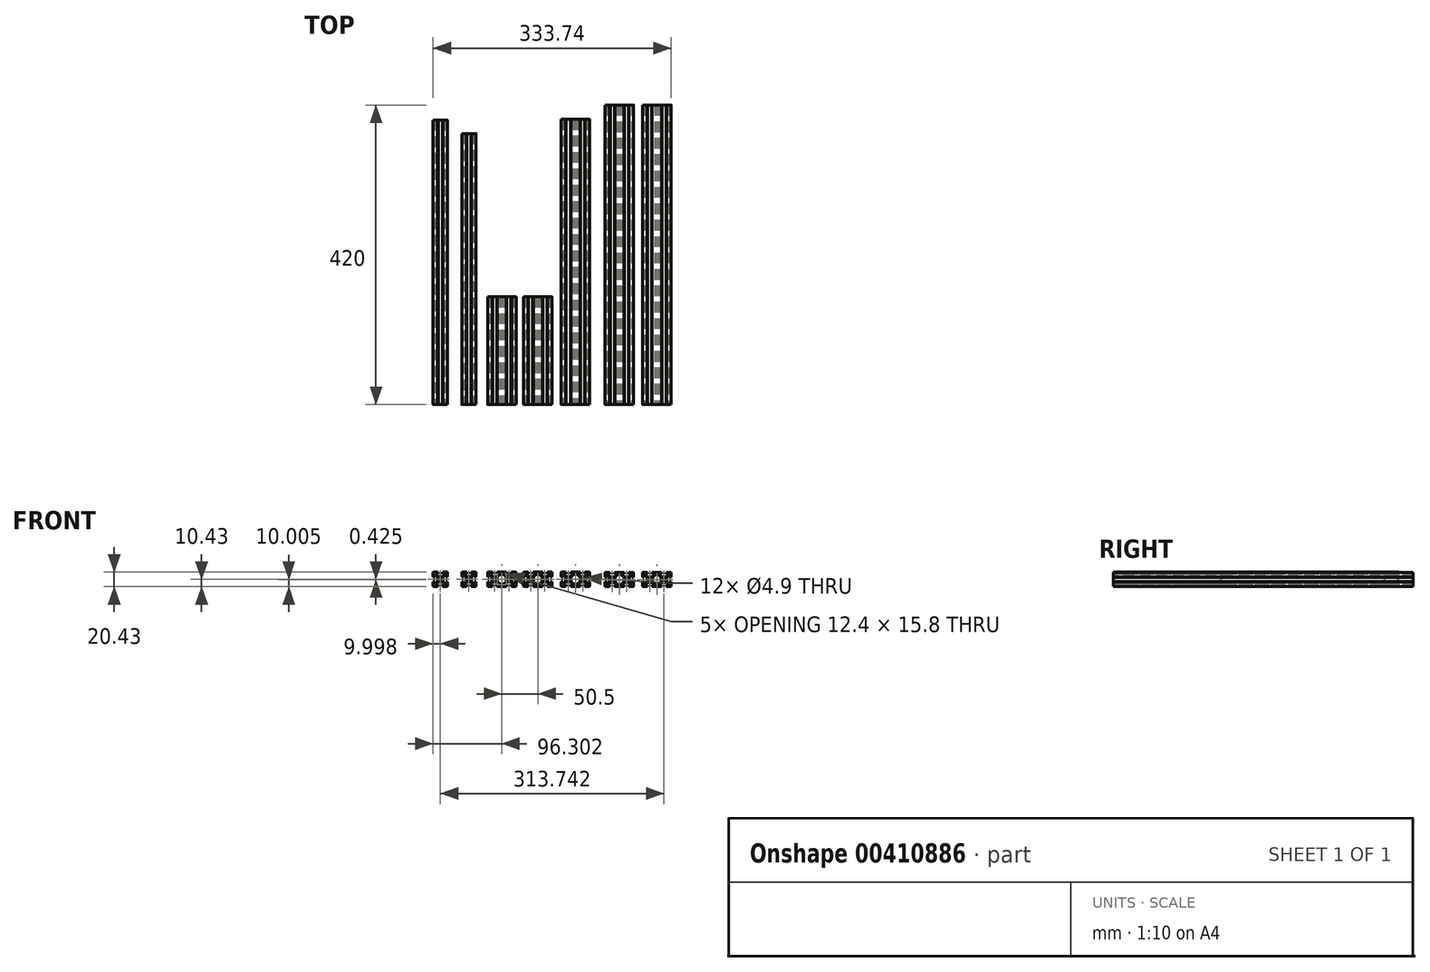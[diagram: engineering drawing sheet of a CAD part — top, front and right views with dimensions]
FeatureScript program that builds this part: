
annotation { "Feature Type Name" : "Feature", "Feature Type Description" : "" }
export const myFeature = defineFeature(function(context is Context, id is Id, definition is map)
    precondition{}
    {
        {
            var Q0;
            Q0=qCreatedBy(makeId("Front.planeOp"),FACE);
            var sketch = newSketch(context, id + "F0", { "sketchPlane" : qUnion([Q0])});
            skCircle(sketch, "E0", {"center": v(-61.2, 10) * mm, "radius": 2.45 * mm});
            skLineSegment(sketch, "E1", {"start": v(-51.2, 0.6) * mm, "end": v(-51.2, 6.4) * mm});
            skLineSegment(sketch, "E2", {"start": v(-51.2, 6.4) * mm, "end": v(-51.8, 6.4) * mm});
            skLineSegment(sketch, "E3", {"start": v(-51.8, 6.4) * mm, "end": v(-51.8, 6.95) * mm});
            skLineSegment(sketch, "E4", {"start": v(-51.8, 6.95) * mm, "end": v(-53.3, 6.95) * mm});
            skLineSegment(sketch, "E5.bottom", {"start": v(-58.31, 6.2) * mm, "end": v(-64.07, 6.2) * mm});
            skLineSegment(sketch, "E5.top", {"start": v(-58.31, 13.8) * mm, "end": v(-64.07, 13.8) * mm});
            skLineSegment(sketch, "E5.left", {"start": v(-57.4, 7.12) * mm, "end": v(-57.4, 12.88) * mm});
            skLineSegment(sketch, "E5.right", {"start": v(-65, 7.12) * mm, "end": v(-65, 12.88) * mm});
            skLineSegment(sketch, "E6", {"start": v(-57.4, 7.12) * mm, "end": v(-53.3, 3.02) * mm});
            skLineSegment(sketch, "E7", {"start": v(-58.31, 6.2) * mm, "end": v(-54.21, 2.1) * mm});
            skLineSegment(sketch, "E8", {"start": v(-53.3, 6.95) * mm, "end": v(-53.3, 3.02) * mm});
            skLineSegment(sketch, "E9.MirrorCS", {"start": v(-58.14, 2.1) * mm, "end": v(-54.21, 2.1) * mm});
            skLineSegment(sketch, "E10.MirrorCS", {"start": v(-58.14, 0.6) * mm, "end": v(-58.14, 2.1) * mm});
            skLineSegment(sketch, "E11.MirrorCS", {"start": v(-57.6, 0.6) * mm, "end": v(-58.14, 0.6) * mm});
            skLineSegment(sketch, "E12.MirrorCS", {"start": v(-57.6, 0) * mm, "end": v(-57.6, 0.6) * mm});
            skLineSegment(sketch, "E13.MirrorCS", {"start": v(-51.8, 0) * mm, "end": v(-57.6, 0) * mm});
            skLineSegment(sketch, "E14", {"start": v(-57.6, 0) * mm, "end": v(-51.8, 0) * mm});
            skLineSegment(sketch, "E15.1.0", {"start": v(-64.24, 2.1) * mm, "end": v(-68.17, 2.1) * mm});
            skLineSegment(sketch, "E15.1.1", {"start": v(-64.24, 0.6) * mm, "end": v(-64.24, 2.1) * mm});
            skLineSegment(sketch, "E15.1.2", {"start": v(-64.8, 0.6) * mm, "end": v(-64.24, 0.6) * mm});
            skLineSegment(sketch, "E15.1.3", {"start": v(-70.6, 0) * mm, "end": v(-64.8, 0) * mm});
            skLineSegment(sketch, "E15.1.4", {"start": v(-64.8, 0) * mm, "end": v(-64.8, 0.6) * mm});
            skLineSegment(sketch, "E15.1.5", {"start": v(-64.07, 6.2) * mm, "end": v(-68.17, 2.1) * mm});
            skLineSegment(sketch, "E15.1.6", {"start": v(-65, 7.12) * mm, "end": v(-69.1, 3.02) * mm});
            skLineSegment(sketch, "E15.1.7", {"start": v(-69.1, 6.95) * mm, "end": v(-69.1, 3.02) * mm});
            skLineSegment(sketch, "E15.1.8", {"start": v(-70.6, 6.95) * mm, "end": v(-69.1, 6.95) * mm});
            skLineSegment(sketch, "E15.1.9", {"start": v(-70.6, 6.4) * mm, "end": v(-70.6, 6.95) * mm});
            skLineSegment(sketch, "E15.1.10", {"start": v(-71.2, 6.4) * mm, "end": v(-70.6, 6.4) * mm});
            skLineSegment(sketch, "E15.1.11", {"start": v(-71.2, 0.6) * mm, "end": v(-71.2, 6.4) * mm});
            skLineSegment(sketch, "E15.2.0", {"start": v(-69.1, 13.05) * mm, "end": v(-69.1, 16.98) * mm});
            skLineSegment(sketch, "E15.2.1", {"start": v(-70.6, 13.05) * mm, "end": v(-69.1, 13.05) * mm});
            skLineSegment(sketch, "E15.2.2", {"start": v(-70.6, 13.6) * mm, "end": v(-70.6, 13.05) * mm});
            skLineSegment(sketch, "E15.2.3", {"start": v(-71.2, 19.4) * mm, "end": v(-71.2, 13.6) * mm});
            skLineSegment(sketch, "E15.2.4", {"start": v(-71.2, 13.6) * mm, "end": v(-70.6, 13.6) * mm});
            skLineSegment(sketch, "E15.2.5", {"start": v(-65, 12.88) * mm, "end": v(-69.1, 16.98) * mm});
            skLineSegment(sketch, "E15.2.6", {"start": v(-64.07, 13.8) * mm, "end": v(-68.17, 17.9) * mm});
            skLineSegment(sketch, "E15.2.7", {"start": v(-64.24, 17.9) * mm, "end": v(-68.17, 17.9) * mm});
            skLineSegment(sketch, "E15.2.8", {"start": v(-64.24, 19.4) * mm, "end": v(-64.24, 17.9) * mm});
            skLineSegment(sketch, "E15.2.9", {"start": v(-64.8, 19.4) * mm, "end": v(-64.24, 19.4) * mm});
            skLineSegment(sketch, "E15.2.10", {"start": v(-64.8, 20) * mm, "end": v(-64.8, 19.4) * mm});
            skLineSegment(sketch, "E15.2.11", {"start": v(-70.6, 20) * mm, "end": v(-64.8, 20) * mm});
            skLineSegment(sketch, "E15.3.0", {"start": v(-58.14, 17.9) * mm, "end": v(-54.21, 17.9) * mm});
            skLineSegment(sketch, "E15.3.1", {"start": v(-58.14, 19.4) * mm, "end": v(-58.14, 17.9) * mm});
            skLineSegment(sketch, "E15.3.2", {"start": v(-57.6, 19.4) * mm, "end": v(-58.14, 19.4) * mm});
            skLineSegment(sketch, "E15.3.3", {"start": v(-51.8, 20) * mm, "end": v(-57.6, 20) * mm});
            skLineSegment(sketch, "E15.3.4", {"start": v(-57.6, 20) * mm, "end": v(-57.6, 19.4) * mm});
            skLineSegment(sketch, "E15.3.5", {"start": v(-58.31, 13.8) * mm, "end": v(-54.21, 17.9) * mm});
            skLineSegment(sketch, "E15.3.6", {"start": v(-57.4, 12.88) * mm, "end": v(-53.3, 16.98) * mm});
            skLineSegment(sketch, "E15.3.7", {"start": v(-53.3, 13.05) * mm, "end": v(-53.3, 16.98) * mm});
            skLineSegment(sketch, "E15.3.8", {"start": v(-51.8, 13.05) * mm, "end": v(-53.3, 13.05) * mm});
            skLineSegment(sketch, "E15.3.9", {"start": v(-51.8, 13.6) * mm, "end": v(-51.8, 13.05) * mm});
            skLineSegment(sketch, "E15.3.10", {"start": v(-51.2, 13.6) * mm, "end": v(-51.8, 13.6) * mm});
            skLineSegment(sketch, "E15.3.11", {"start": v(-51.2, 19.4) * mm, "end": v(-51.2, 13.6) * mm});
            skLineSegment(sketch, "E15.anchor1", {"start": v(-59.82, 6.2) * mm, "end": v(-57.6, 0) * mm, "construction": true});
            skLineSegment(sketch, "E15.anchor2", {"start": v(-61.2, 10) * mm, "end": v(-51.2, 13.6) * mm, "construction": true});
            skPoint(sketch, "E16.orphan", {"position": v(-57.4, 13.8) * mm});
            skPoint(sketch, "E17.orphan", {"position": v(-65, 6.2) * mm});
            skArc(sketch, "E18", {"start": v(-51.8, 0) * mm, "mid": v(-51.37, 0.18) * mm, "end": v(-51.2, 0.6) * mm});
            skArc(sketch, "E19.1.6", {"start": v(-71.2, 0.6) * mm, "mid": v(-71.02, 0.18) * mm, "end": v(-70.6, 0) * mm});
            skLineSegment(sketch, "E19.1.7", {"start": v(-71.2, 6.4) * mm, "end": v(-71.2, 0.6) * mm});
            skArc(sketch, "E19.2.6", {"start": v(-70.6, 20) * mm, "mid": v(-71.02, 19.82) * mm, "end": v(-71.2, 19.4) * mm});
            skLineSegment(sketch, "E19.2.7", {"start": v(-64.8, 20) * mm, "end": v(-70.6, 20) * mm});
            skArc(sketch, "E19.3.6", {"start": v(-51.2, 19.4) * mm, "mid": v(-51.37, 19.82) * mm, "end": v(-51.8, 20) * mm});
            skLineSegment(sketch, "E19.3.7", {"start": v(-51.2, 13.6) * mm, "end": v(-51.2, 19.4) * mm});
            skLineSegment(sketch, "E19.anchor1", {"start": v(-61.2, 10) * mm, "end": v(-53.3, 3.02) * mm, "construction": true});
            skLineSegment(sketch, "E19.anchor2", {"start": v(-61.2, 10) * mm, "end": v(-54.21, 17.9) * mm, "construction": true});
            skSolve(sketch);
        }
        {
            var Q0;
            Q0=makeQuery(id+"F0.imprint","IMPRINT",FACE,{"disambiguationData":[TD([[makeQuery(id+"F0.imprint","IMPRINT",EDGE,{"derivedFrom":sQuery(id+"F0.wireOp",EDGE,"E0")}),-1.0]])]});
            extrude(context, id + "F1", {"entities" : qUnion([Q0]), "oppositeDirection" : true, "depth" : 399 * mm});
        }
        {
            var Q0;
            Q0=qCreatedBy(makeId("Front.planeOp"),FACE);
            var sketch = newSketch(context, id + "F2", { "sketchPlane" : qUnion([Q0])});
            skCircle(sketch, "E20", {"center": v(-21.06, 10) * mm, "radius": 2.45 * mm});
            skLineSegment(sketch, "E21", {"start": v(-11.06, 0.6) * mm, "end": v(-11.06, 6.4) * mm});
            skLineSegment(sketch, "E22", {"start": v(-11.06, 6.4) * mm, "end": v(-11.66, 6.4) * mm});
            skLineSegment(sketch, "E23", {"start": v(-11.66, 6.4) * mm, "end": v(-11.66, 6.94) * mm});
            skLineSegment(sketch, "E24", {"start": v(-11.66, 6.94) * mm, "end": v(-13.16, 6.94) * mm});
            skLineSegment(sketch, "E25.bottom", {"start": v(-18.18, 6.2) * mm, "end": v(-23.94, 6.2) * mm});
            skLineSegment(sketch, "E25.top", {"start": v(-18.18, 13.8) * mm, "end": v(-23.94, 13.8) * mm});
            skLineSegment(sketch, "E25.left", {"start": v(-17.26, 7.11) * mm, "end": v(-17.26, 12.87) * mm});
            skLineSegment(sketch, "E25.right", {"start": v(-24.86, 7.11) * mm, "end": v(-24.86, 12.87) * mm});
            skLineSegment(sketch, "E26", {"start": v(-17.26, 7.11) * mm, "end": v(-13.16, 3.01) * mm});
            skLineSegment(sketch, "E27", {"start": v(-18.18, 6.2) * mm, "end": v(-14.08, 2.1) * mm});
            skLineSegment(sketch, "E28", {"start": v(-13.16, 6.94) * mm, "end": v(-13.16, 3.01) * mm});
            skLineSegment(sketch, "E29.MirrorCS", {"start": v(-18.01, 2.1) * mm, "end": v(-14.08, 2.1) * mm});
            skLineSegment(sketch, "E30.MirrorCS", {"start": v(-18.01, 0.6) * mm, "end": v(-18.01, 2.1) * mm});
            skLineSegment(sketch, "E31.MirrorCS", {"start": v(-17.46, 0) * mm, "end": v(-17.46, 0.6) * mm});
            skLineSegment(sketch, "E32", {"start": v(-17.46, 0) * mm, "end": v(-11.66, 0) * mm});
            skLineSegment(sketch, "E33.1.0", {"start": v(-24.11, 2.1) * mm, "end": v(-28.04, 2.1) * mm});
            skLineSegment(sketch, "E33.1.1", {"start": v(-24.11, 0.6) * mm, "end": v(-24.11, 2.1) * mm});
            skLineSegment(sketch, "E33.1.2", {"start": v(-24.66, 0.6) * mm, "end": v(-24.11, 0.6) * mm});
            skLineSegment(sketch, "E33.1.3", {"start": v(-30.46, 0) * mm, "end": v(-24.66, 0) * mm});
            skLineSegment(sketch, "E33.1.4", {"start": v(-24.66, 0) * mm, "end": v(-24.66, 0.6) * mm});
            skLineSegment(sketch, "E33.1.5", {"start": v(-23.94, 6.2) * mm, "end": v(-28.04, 2.1) * mm});
            skLineSegment(sketch, "E33.1.6", {"start": v(-24.86, 7.11) * mm, "end": v(-28.96, 3.01) * mm});
            skLineSegment(sketch, "E33.2.0", {"start": v(-28.96, 3.01) * mm, "end": v(-28.96, 6.94) * mm});
            skLineSegment(sketch, "E33.2.3", {"start": v(-31.06, 19.4) * mm, "end": v(-31.06, 13.6) * mm});
            skLineSegment(sketch, "E33.2.5", {"start": v(-24.86, 12.87) * mm, "end": v(-28.96, 16.97) * mm});
            skLineSegment(sketch, "E33.2.6", {"start": v(-23.94, 13.8) * mm, "end": v(-28.04, 17.9) * mm});
            skLineSegment(sketch, "E33.2.11", {"start": v(-30.46, 20) * mm, "end": v(-24.66, 20) * mm});
            skLineSegment(sketch, "E33.3.0", {"start": v(-18.01, 17.9) * mm, "end": v(-14.08, 17.9) * mm});
            skLineSegment(sketch, "E33.3.1", {"start": v(-18.01, 19.4) * mm, "end": v(-18.01, 17.9) * mm});
            skLineSegment(sketch, "E33.3.2", {"start": v(-17.46, 19.4) * mm, "end": v(-18.01, 19.4) * mm});
            skLineSegment(sketch, "E33.3.3", {"start": v(-11.66, 20) * mm, "end": v(-17.46, 20) * mm});
            skLineSegment(sketch, "E33.3.4", {"start": v(-17.46, 20) * mm, "end": v(-17.46, 19.4) * mm});
            skLineSegment(sketch, "E33.3.5", {"start": v(-18.18, 13.8) * mm, "end": v(-14.08, 17.9) * mm});
            skLineSegment(sketch, "E33.3.6", {"start": v(-17.26, 12.87) * mm, "end": v(-13.16, 16.97) * mm});
            skLineSegment(sketch, "E33.3.7", {"start": v(-13.16, 13.04) * mm, "end": v(-13.16, 16.97) * mm});
            skLineSegment(sketch, "E33.3.11", {"start": v(-11.06, 19.4) * mm, "end": v(-11.06, 13.6) * mm});
            skArc(sketch, "E34", {"start": v(-11.66, 0) * mm, "mid": v(-11.24, 0.17) * mm, "end": v(-11.06, 0.6) * mm});
            skArc(sketch, "E35.1.6", {"start": v(-31.06, 0.6) * mm, "mid": v(-30.89, 0.17) * mm, "end": v(-30.46, 0) * mm});
            skLineSegment(sketch, "E35.1.7", {"start": v(-31.06, 6.4) * mm, "end": v(-31.06, 0.6) * mm});
            skLineSegment(sketch, "E35.1.8", {"start": v(-31.06, 6.4) * mm, "end": v(-30.46, 6.4) * mm});
            skLineSegment(sketch, "E35.1.9", {"start": v(-30.46, 6.4) * mm, "end": v(-30.46, 6.94) * mm});
            skLineSegment(sketch, "E35.1.10", {"start": v(-30.46, 6.94) * mm, "end": v(-28.96, 6.94) * mm});
            skLineSegment(sketch, "E35.1.11", {"start": v(-28.96, 6.94) * mm, "end": v(-28.96, 3.01) * mm});
            skLineSegment(sketch, "E35.2.1", {"start": v(-28.96, 13.04) * mm, "end": v(-28.96, 16.97) * mm});
            skLineSegment(sketch, "E35.2.2", {"start": v(-30.46, 13.04) * mm, "end": v(-28.96, 13.04) * mm});
            skLineSegment(sketch, "E35.2.3", {"start": v(-30.46, 13.6) * mm, "end": v(-30.46, 13.04) * mm});
            skLineSegment(sketch, "E35.2.4", {"start": v(-31.06, 13.6) * mm, "end": v(-30.46, 13.6) * mm});
            skArc(sketch, "E35.2.6", {"start": v(-30.46, 20) * mm, "mid": v(-30.89, 19.82) * mm, "end": v(-31.06, 19.4) * mm});
            skLineSegment(sketch, "E35.2.7", {"start": v(-24.66, 20) * mm, "end": v(-30.46, 20) * mm});
            skLineSegment(sketch, "E35.2.8", {"start": v(-24.66, 20) * mm, "end": v(-24.66, 19.4) * mm});
            skLineSegment(sketch, "E35.2.9", {"start": v(-24.66, 19.4) * mm, "end": v(-24.11, 19.4) * mm});
            skLineSegment(sketch, "E35.2.10", {"start": v(-24.11, 19.4) * mm, "end": v(-24.11, 17.9) * mm});
            skLineSegment(sketch, "E35.2.11", {"start": v(-24.11, 17.9) * mm, "end": v(-28.04, 17.9) * mm});
            skArc(sketch, "E35.3.6", {"start": v(-11.06, 19.4) * mm, "mid": v(-11.24, 19.82) * mm, "end": v(-11.66, 20) * mm});
            skLineSegment(sketch, "E35.3.7", {"start": v(-11.06, 13.6) * mm, "end": v(-11.06, 19.4) * mm});
            skLineSegment(sketch, "E35.3.8", {"start": v(-11.06, 13.6) * mm, "end": v(-11.66, 13.6) * mm});
            skLineSegment(sketch, "E35.3.9", {"start": v(-11.66, 13.6) * mm, "end": v(-11.66, 13.04) * mm});
            skLineSegment(sketch, "E35.3.10", {"start": v(-11.66, 13.04) * mm, "end": v(-13.16, 13.04) * mm});
            skLineSegment(sketch, "E35.3.11", {"start": v(-13.16, 3.01) * mm, "end": v(-13.16, 6.94) * mm});
            skLineSegment(sketch, "E36.trimOffspring", {"start": v(-31.06, 6.4) * mm, "end": v(-31.06, 2.99) * mm});
            skLineSegment(sketch, "E37.trimOffspring", {"start": v(-11.06, 6.4) * mm, "end": v(-11.06, 2.99) * mm});
            skLineSegment(sketch, "E38.trimOffspring", {"start": v(-14.08, 17.9) * mm, "end": v(-18.01, 17.9) * mm});
            skLineSegment(sketch, "E39", {"start": v(-17.46, 0.6) * mm, "end": v(-18.01, 0.6) * mm});
            skLineSegment(sketch, "E40.trimOffspring", {"start": v(-14.08, 2.1) * mm, "end": v(-18.18, 6.2) * mm});
            skSolve(sketch);
        }
        {
            var Q0;
            Q0=makeQuery(id+"F2.imprint","IMPRINT",FACE,{"disambiguationData":[TD([[makeQuery(id+"F2.imprint","IMPRINT",EDGE,{"derivedFrom":sQuery(id+"F2.wireOp",EDGE,"E20")}),-1.0]])]});
            extrude(context, id + "F3", {"entities" : qUnion([Q0]), "oppositeDirection" : true, "depth" : 380 * mm});
        }
        {
            var Q0;
            Q0=qCreatedBy(makeId("Front.planeOp"),FACE);
            var sketch = newSketch(context, id + "F4", { "sketchPlane" : qUnion([Q0])});
            skCircle(sketch, "E41", {"center": v(15.11, 10) * mm, "radius": 2.45 * mm});
            skLineSegment(sketch, "E42.bottom", {"start": v(18, 6.2) * mm, "end": v(12.23, 6.2) * mm});
            skLineSegment(sketch, "E42.top", {"start": v(18, 13.8) * mm, "end": v(12.23, 13.8) * mm});
            skLineSegment(sketch, "E42.left", {"start": v(18.91, 7.12) * mm, "end": v(18.91, 12.88) * mm});
            skLineSegment(sketch, "E42.right", {"start": v(11.31, 7.12) * mm, "end": v(11.31, 12.88) * mm});
            skLineSegment(sketch, "E43", {"start": v(18.91, 7.12) * mm, "end": v(23.01, 3.02) * mm});
            skLineSegment(sketch, "E44", {"start": v(18, 6.2) * mm, "end": v(22.1, 2.1) * mm});
            skLineSegment(sketch, "E45.MirrorCS", {"start": v(18.16, 2.1) * mm, "end": v(22.1, 2.1) * mm});
            skLineSegment(sketch, "E46.MirrorCS", {"start": v(18.16, 0.6) * mm, "end": v(18.16, 2.1) * mm});
            skLineSegment(sketch, "E47.MirrorCS", {"start": v(18.71, 0) * mm, "end": v(18.71, 0.6) * mm});
            skLineSegment(sketch, "E48", {"start": v(18.71, 0) * mm, "end": v(24.51, 0) * mm});
            skLineSegment(sketch, "E49.1.0", {"start": v(12.06, 2.1) * mm, "end": v(8.13, 2.1) * mm});
            skLineSegment(sketch, "E49.1.1", {"start": v(12.06, 0.6) * mm, "end": v(12.06, 2.1) * mm});
            skLineSegment(sketch, "E49.1.2", {"start": v(11.51, 0.6) * mm, "end": v(12.06, 0.6) * mm});
            skLineSegment(sketch, "E49.1.3", {"start": v(5.71, 0) * mm, "end": v(11.51, 0) * mm});
            skLineSegment(sketch, "E49.1.4", {"start": v(11.51, 0) * mm, "end": v(11.51, 0.6) * mm});
            skLineSegment(sketch, "E49.1.5", {"start": v(12.23, 6.2) * mm, "end": v(8.13, 2.1) * mm});
            skLineSegment(sketch, "E49.1.6", {"start": v(11.31, 7.12) * mm, "end": v(7.21, 3.02) * mm});
            skLineSegment(sketch, "E49.2.0", {"start": v(7.21, 3.02) * mm, "end": v(7.21, 6.95) * mm});
            skLineSegment(sketch, "E49.2.3", {"start": v(5.11, 19.4) * mm, "end": v(5.11, 13.6) * mm});
            skLineSegment(sketch, "E49.2.5", {"start": v(11.31, 12.88) * mm, "end": v(7.21, 16.98) * mm});
            skLineSegment(sketch, "E49.2.6", {"start": v(12.23, 13.8) * mm, "end": v(8.13, 17.9) * mm});
            skLineSegment(sketch, "E49.2.11", {"start": v(5.71, 20) * mm, "end": v(11.51, 20) * mm});
            skLineSegment(sketch, "E49.3.0", {"start": v(18.16, 17.9) * mm, "end": v(22.1, 17.9) * mm});
            skLineSegment(sketch, "E49.3.1", {"start": v(18.16, 19.4) * mm, "end": v(18.16, 17.9) * mm});
            skLineSegment(sketch, "E49.3.2", {"start": v(18.71, 19.4) * mm, "end": v(18.16, 19.4) * mm});
            skLineSegment(sketch, "E49.3.3", {"start": v(24.51, 20) * mm, "end": v(18.71, 20) * mm});
            skLineSegment(sketch, "E49.3.4", {"start": v(18.71, 20) * mm, "end": v(18.71, 19.4) * mm});
            skLineSegment(sketch, "E49.3.5", {"start": v(18, 13.8) * mm, "end": v(22.1, 17.9) * mm});
            skLineSegment(sketch, "E49.3.6", {"start": v(18.91, 12.88) * mm, "end": v(23.01, 16.98) * mm});
            skArc(sketch, "E50.1.6", {"start": v(5.11, 0.6) * mm, "mid": v(5.29, 0.18) * mm, "end": v(5.71, 0) * mm});
            skLineSegment(sketch, "E50.1.7", {"start": v(5.11, 6.4) * mm, "end": v(5.11, 0.6) * mm});
            skLineSegment(sketch, "E50.1.8", {"start": v(5.11, 6.4) * mm, "end": v(5.71, 6.4) * mm});
            skLineSegment(sketch, "E50.1.9", {"start": v(5.71, 6.4) * mm, "end": v(5.71, 6.95) * mm});
            skLineSegment(sketch, "E50.1.10", {"start": v(5.71, 6.95) * mm, "end": v(7.21, 6.95) * mm});
            skLineSegment(sketch, "E50.1.11", {"start": v(7.21, 6.95) * mm, "end": v(7.21, 3.02) * mm});
            skLineSegment(sketch, "E50.2.1", {"start": v(7.21, 13.05) * mm, "end": v(7.21, 16.98) * mm});
            skLineSegment(sketch, "E50.2.2", {"start": v(5.71, 13.05) * mm, "end": v(7.21, 13.05) * mm});
            skLineSegment(sketch, "E50.2.3", {"start": v(5.71, 13.6) * mm, "end": v(5.71, 13.05) * mm});
            skLineSegment(sketch, "E50.2.4", {"start": v(5.11, 13.6) * mm, "end": v(5.71, 13.6) * mm});
            skArc(sketch, "E50.2.6", {"start": v(5.71, 20) * mm, "mid": v(5.29, 19.82) * mm, "end": v(5.11, 19.4) * mm});
            skLineSegment(sketch, "E50.2.7", {"start": v(11.51, 20) * mm, "end": v(5.71, 20) * mm});
            skLineSegment(sketch, "E50.2.8", {"start": v(11.51, 20) * mm, "end": v(11.51, 19.4) * mm});
            skLineSegment(sketch, "E50.2.9", {"start": v(11.51, 19.4) * mm, "end": v(12.06, 19.4) * mm});
            skLineSegment(sketch, "E50.2.10", {"start": v(12.06, 19.4) * mm, "end": v(12.06, 17.9) * mm});
            skLineSegment(sketch, "E50.2.11", {"start": v(12.06, 17.9) * mm, "end": v(8.13, 17.9) * mm});
            skLineSegment(sketch, "E51.trimOffspring", {"start": v(5.11, 6.4) * mm, "end": v(5.11, 3) * mm});
            skLineSegment(sketch, "E52.trimOffspring", {"start": v(22.1, 17.9) * mm, "end": v(18.16, 17.9) * mm});
            skLineSegment(sketch, "E53", {"start": v(18.71, 0.6) * mm, "end": v(18.16, 0.6) * mm});
            skLineSegment(sketch, "E54.trimOffspring", {"start": v(22.1, 2.1) * mm, "end": v(18, 6.2) * mm});
            skLineSegment(sketch, "E55.MirrorCS", {"start": v(38.16, 0.6) * mm, "end": v(38.16, 2.1) * mm});
            skLineSegment(sketch, "E56.MirrorCS", {"start": v(31.51, 19.4) * mm, "end": v(32.06, 19.4) * mm});
            skLineSegment(sketch, "E57.MirrorCS", {"start": v(38.71, 0.6) * mm, "end": v(38.16, 0.6) * mm});
            skLineSegment(sketch, "E58.MirrorCS", {"start": v(38.71, 0) * mm, "end": v(38.71, 0.6) * mm});
            skLineSegment(sketch, "E59.MirrorCS", {"start": v(31.51, 20) * mm, "end": v(31.51, 19.4) * mm});
            skLineSegment(sketch, "E60.MirrorCS", {"start": v(32.06, 19.4) * mm, "end": v(32.06, 17.9) * mm});
            skLineSegment(sketch, "E61.MirrorCS", {"start": v(38.71, 20) * mm, "end": v(38.71, 19.4) * mm});
            skArc(sketch, "E62.MirrorCS", {"start": v(44.51, 20) * mm, "mid": v(44.94, 19.82) * mm, "end": v(45.11, 19.4) * mm});
            skLineSegment(sketch, "E63.MirrorCS", {"start": v(45.11, 13.6) * mm, "end": v(44.51, 13.6) * mm});
            skLineSegment(sketch, "E64.MirrorCS", {"start": v(38.71, 19.4) * mm, "end": v(38.16, 19.4) * mm});
            skLineSegment(sketch, "E65.MirrorCS", {"start": v(45.11, 6.4) * mm, "end": v(44.51, 6.4) * mm});
            skLineSegment(sketch, "E66.MirrorCS", {"start": v(44.51, 13.05) * mm, "end": v(43.01, 13.05) * mm});
            skLineSegment(sketch, "E67.MirrorCS", {"start": v(32.06, 0.6) * mm, "end": v(32.06, 2.1) * mm});
            skLineSegment(sketch, "E68.MirrorCS", {"start": v(38.16, 19.4) * mm, "end": v(38.16, 17.9) * mm});
            skArc(sketch, "E69.MirrorCS", {"start": v(45.11, 0.6) * mm, "mid": v(44.94, 0.18) * mm, "end": v(44.51, 0) * mm});
            skLineSegment(sketch, "E70.MirrorCS", {"start": v(32.06, 17.9) * mm, "end": v(28.13, 17.9) * mm});
            skLineSegment(sketch, "E71.MirrorCS", {"start": v(31.51, 0.6) * mm, "end": v(32.06, 0.6) * mm});
            skLineSegment(sketch, "E72.MirrorCS", {"start": v(44.51, 6.4) * mm, "end": v(44.51, 6.95) * mm});
            skLineSegment(sketch, "E73.MirrorCS", {"start": v(44.51, 6.95) * mm, "end": v(43.01, 6.95) * mm});
            skLineSegment(sketch, "E74.MirrorCS", {"start": v(31.51, 0) * mm, "end": v(31.51, 0.6) * mm});
            skLineSegment(sketch, "E75.MirrorCS", {"start": v(44.51, 13.6) * mm, "end": v(44.51, 13.05) * mm});
            skLineSegment(sketch, "E76.MirrorCS", {"start": v(32.23, 13.8) * mm, "end": v(28.13, 17.9) * mm});
            skPoint(sketch, "E77.MirrorP", {"position": v(35.11, 10) * mm});
            skLineSegment(sketch, "E78.MirrorCS", {"start": v(43.01, 13.05) * mm, "end": v(43.01, 16.98) * mm});
            skLineSegment(sketch, "E79.MirrorCS", {"start": v(44.51, 0) * mm, "end": v(38.71, 0) * mm});
            skLineSegment(sketch, "E80.MirrorCS", {"start": v(38.16, 17.9) * mm, "end": v(42.1, 17.9) * mm});
            skLineSegment(sketch, "E81.MirrorCS", {"start": v(38.91, 7.12) * mm, "end": v(43.01, 3.02) * mm});
            skLineSegment(sketch, "E82.MirrorCS", {"start": v(38.16, 2.1) * mm, "end": v(42.1, 2.1) * mm});
            skLineSegment(sketch, "E83.MirrorCS", {"start": v(38.91, 12.88) * mm, "end": v(43.01, 16.98) * mm});
            skLineSegment(sketch, "E84.MirrorCS", {"start": v(43.01, 6.95) * mm, "end": v(43.01, 3.02) * mm});
            skLineSegment(sketch, "E85.MirrorCS", {"start": v(38, 6.2) * mm, "end": v(42.1, 2.1) * mm});
            skLineSegment(sketch, "E86.MirrorCS", {"start": v(28.13, 17.9) * mm, "end": v(32.06, 17.9) * mm});
            skLineSegment(sketch, "E87.MirrorCS", {"start": v(38.71, 20) * mm, "end": v(44.51, 20) * mm});
            skLineSegment(sketch, "E88.MirrorCS", {"start": v(38, 13.8) * mm, "end": v(42.1, 17.9) * mm});
            skLineSegment(sketch, "E89.MirrorCS", {"start": v(45.11, 6.4) * mm, "end": v(45.11, 3) * mm});
            skLineSegment(sketch, "E90.MirrorCS", {"start": v(25.71, 20) * mm, "end": v(31.51, 20) * mm});
            skLineSegment(sketch, "E91.MirrorCS", {"start": v(45.11, 19.4) * mm, "end": v(45.11, 13.6) * mm});
            skLineSegment(sketch, "E92.MirrorCS", {"start": v(28.13, 2.1) * mm, "end": v(32.23, 6.2) * mm});
            skLineSegment(sketch, "E93.MirrorCS", {"start": v(43.01, 3.02) * mm, "end": v(43.01, 6.95) * mm});
            skLineSegment(sketch, "E94.MirrorCS", {"start": v(31.31, 12.88) * mm, "end": v(27.21, 16.98) * mm});
            skLineSegment(sketch, "E95.MirrorCS", {"start": v(31.51, 0) * mm, "end": v(25.71, 0) * mm});
            skCircle(sketch, "E96.MirrorC", {"center": v(35.11, 10) * mm, "radius": 2.45 * mm});
            skLineSegment(sketch, "E97.MirrorCS", {"start": v(32.23, 13.8) * mm, "end": v(38, 13.8) * mm});
            skLineSegment(sketch, "E98.MirrorCS", {"start": v(31.31, 7.12) * mm, "end": v(31.31, 12.88) * mm});
            skLineSegment(sketch, "E99.MirrorCS", {"start": v(38.91, 7.12) * mm, "end": v(38.91, 12.88) * mm});
            skLineSegment(sketch, "E100.MirrorCS", {"start": v(31.31, 7.12) * mm, "end": v(27.21, 3.02) * mm});
            skLineSegment(sketch, "E101.MirrorCS", {"start": v(32.23, 6.2) * mm, "end": v(28.13, 2.1) * mm});
            skLineSegment(sketch, "E102.MirrorCS", {"start": v(32.06, 2.1) * mm, "end": v(28.13, 2.1) * mm});
            skLineSegment(sketch, "E103.MirrorCS", {"start": v(45.11, 6.4) * mm, "end": v(45.11, 0.6) * mm});
            skLineSegment(sketch, "E104.MirrorCS", {"start": v(44.51, 20) * mm, "end": v(38.71, 20) * mm});
            skLineSegment(sketch, "E105.MirrorCS", {"start": v(32.23, 6.2) * mm, "end": v(38, 6.2) * mm});
            skLineSegment(sketch, "E106", {"start": v(23.93, 17.9) * mm, "end": v(26.3, 17.9) * mm});
            skLineSegment(sketch, "E107", {"start": v(23.01, 16.98) * mm, "end": v(23.93, 17.9) * mm});
            skLineSegment(sketch, "E108", {"start": v(27.21, 16.98) * mm, "end": v(26.3, 17.9) * mm});
            skLineSegment(sketch, "E109", {"start": v(24.51, 20) * mm, "end": v(25.71, 20) * mm});
            skPoint(sketch, "E50.3.6.start.orphan", {"position": v(25.11, 19.4) * mm});
            skLineSegment(sketch, "E110", {"start": v(23.93, 2.1) * mm, "end": v(26.3, 2.1) * mm});
            skLineSegment(sketch, "E111", {"start": v(27.21, 3.02) * mm, "end": v(26.3, 2.1) * mm});
            skLineSegment(sketch, "E112", {"start": v(23.01, 3.02) * mm, "end": v(23.93, 2.1) * mm});
            skLineSegment(sketch, "E113", {"start": v(24.51, 0) * mm, "end": v(25.71, 0) * mm});
            skSolve(sketch);
        }
        {
            var Q0;
            Q0=makeQuery(id+"F4.imprint","IMPRINT",FACE,{"disambiguationData":[TD([[makeQuery(id+"F4.imprint","IMPRINT",EDGE,{"derivedFrom":sQuery(id+"F4.wireOp",EDGE,"E41")}),-1.0]])]});
            extrude(context, id + "F5", {"entities" : qUnion([Q0]), "oppositeDirection" : true, "depth" : 151 * mm});
        }
        {
            var Q0;
            Q0=makeQuery(id+"F5.opExtrude","SWEPT_BODY",BODY,{"disambiguationData":[OSD([sQuery(id+"F4.wireOp",EDGE,"E41"),sQuery(id+"F4.wireOp",EDGE,"E42.bottom"),sQuery(id+"F4.wireOp",EDGE,"E42.top"),sQuery(id+"F4.wireOp",EDGE,"E42.left"),sQuery(id+"F4.wireOp",EDGE,"E42.right"),sQuery(id+"F4.wireOp",EDGE,"E43"),sQuery(id+"F4.wireOp",EDGE,"E45.MirrorCS"),sQuery(id+"F4.wireOp",EDGE,"E46.MirrorCS"),sQuery(id+"F4.wireOp",EDGE,"E47.MirrorCS"),sQuery(id+"F4.wireOp",EDGE,"E48"),sQuery(id+"F4.wireOp",EDGE,"E49.3.6"),sQuery(id+"F4.wireOp",EDGE,"E49.1.0"),sQuery(id+"F4.wireOp",EDGE,"E49.1.1"),sQuery(id+"F4.wireOp",EDGE,"E49.1.2"),sQuery(id+"F4.wireOp",EDGE,"E49.1.4"),sQuery(id+"F4.wireOp",EDGE,"E49.1.3"),sQuery(id+"F4.wireOp",EDGE,"E50.1.6"),sQuery(id+"F4.wireOp",EDGE,"E50.1.7"),sQuery(id+"F4.wireOp",EDGE,"E50.1.8"),sQuery(id+"F4.wireOp",EDGE,"E50.1.9"),sQuery(id+"F4.wireOp",EDGE,"E50.1.10"),sQuery(id+"F4.wireOp",EDGE,"E50.1.11"),sQuery(id+"F4.wireOp",EDGE,"E49.1.6"),sQuery(id+"F4.wireOp",EDGE,"E50.2.2"),sQuery(id+"F4.wireOp",EDGE,"E50.2.3"),sQuery(id+"F4.wireOp",EDGE,"E50.2.4"),sQuery(id+"F4.wireOp",EDGE,"E49.2.3"),sQuery(id+"F4.wireOp",EDGE,"E50.2.6"),sQuery(id+"F4.wireOp",EDGE,"E50.2.7"),sQuery(id+"F4.wireOp",EDGE,"E50.2.8"),sQuery(id+"F4.wireOp",EDGE,"E50.2.9"),sQuery(id+"F4.wireOp",EDGE,"E50.2.10"),sQuery(id+"F4.wireOp",EDGE,"E49.2.6"),sQuery(id+"F4.wireOp",EDGE,"E49.3.5"),sQuery(id+"F4.wireOp",EDGE,"E49.3.1"),sQuery(id+"F4.wireOp",EDGE,"E49.3.2"),sQuery(id+"F4.wireOp",EDGE,"E49.3.4"),sQuery(id+"F4.wireOp",EDGE,"E49.3.3"),sQuery(id+"F4.wireOp",EDGE,"E51.trimOffspring"),sQuery(id+"F4.wireOp",EDGE,"E50.2.1"),sQuery(id+"F4.wireOp",EDGE,"E50.2.11"),sQuery(id+"F4.wireOp",EDGE,"E49.2.5"),sQuery(id+"F4.wireOp",EDGE,"E49.1.5"),sQuery(id+"F4.wireOp",EDGE,"E52.trimOffspring"),sQuery(id+"F4.wireOp",EDGE,"E53"),sQuery(id+"F4.wireOp",EDGE,"E54.trimOffspring"),sQuery(id+"F4.wireOp",EDGE,"E55.MirrorCS"),sQuery(id+"F4.wireOp",EDGE,"E57.MirrorCS"),sQuery(id+"F4.wireOp",EDGE,"E59.MirrorCS"),sQuery(id+"F4.wireOp",EDGE,"E56.MirrorCS"),sQuery(id+"F4.wireOp",EDGE,"E60.MirrorCS"),sQuery(id+"F4.wireOp",EDGE,"E58.MirrorCS"),sQuery(id+"F4.wireOp",EDGE,"E61.MirrorCS"),sQuery(id+"F4.wireOp",EDGE,"E62.MirrorCS"),sQuery(id+"F4.wireOp",EDGE,"E63.MirrorCS"),sQuery(id+"F4.wireOp",EDGE,"E64.MirrorCS"),sQuery(id+"F4.wireOp",EDGE,"E65.MirrorCS"),sQuery(id+"F4.wireOp",EDGE,"E66.MirrorCS"),sQuery(id+"F4.wireOp",EDGE,"E67.MirrorCS"),sQuery(id+"F4.wireOp",EDGE,"E68.MirrorCS"),sQuery(id+"F4.wireOp",EDGE,"E69.MirrorCS"),sQuery(id+"F4.wireOp",EDGE,"E71.MirrorCS"),sQuery(id+"F4.wireOp",EDGE,"E72.MirrorCS"),sQuery(id+"F4.wireOp",EDGE,"E73.MirrorCS"),sQuery(id+"F4.wireOp",EDGE,"E74.MirrorCS"),sQuery(id+"F4.wireOp",EDGE,"E75.MirrorCS"),sQuery(id+"F4.wireOp",EDGE,"E93.MirrorCS"),sQuery(id+"F4.wireOp",EDGE,"E91.MirrorCS"),sQuery(id+"F4.wireOp",EDGE,"E81.MirrorCS"),sQuery(id+"F4.wireOp",EDGE,"E94.MirrorCS"),sQuery(id+"F4.wireOp",EDGE,"E95.MirrorCS"),sQuery(id+"F4.wireOp",EDGE,"E96.MirrorC"),sQuery(id+"F4.wireOp",EDGE,"E78.MirrorCS"),sQuery(id+"F4.wireOp",EDGE,"E97.MirrorCS"),sQuery(id+"F4.wireOp",EDGE,"E98.MirrorCS"),sQuery(id+"F4.wireOp",EDGE,"E99.MirrorCS"),sQuery(id+"F4.wireOp",EDGE,"E100.MirrorCS"),sQuery(id+"F4.wireOp",EDGE,"E101.MirrorCS"),sQuery(id+"F4.wireOp",EDGE,"E88.MirrorCS"),sQuery(id+"F4.wireOp",EDGE,"E102.MirrorCS"),sQuery(id+"F4.wireOp",EDGE,"E70.MirrorCS"),sQuery(id+"F4.wireOp",EDGE,"E103.MirrorCS"),sQuery(id+"F4.wireOp",EDGE,"E82.MirrorCS"),sQuery(id+"F4.wireOp",EDGE,"E83.MirrorCS"),sQuery(id+"F4.wireOp",EDGE,"E85.MirrorCS"),sQuery(id+"F4.wireOp",EDGE,"E80.MirrorCS"),sQuery(id+"F4.wireOp",EDGE,"E76.MirrorCS"),sQuery(id+"F4.wireOp",EDGE,"E79.MirrorCS"),sQuery(id+"F4.wireOp",EDGE,"E90.MirrorCS"),sQuery(id+"F4.wireOp",EDGE,"E104.MirrorCS"),sQuery(id+"F4.wireOp",EDGE,"E105.MirrorCS"),sQuery(id+"F4.wireOp",EDGE,"E106"),sQuery(id+"F4.wireOp",EDGE,"E107"),sQuery(id+"F4.wireOp",EDGE,"E108"),sQuery(id+"F4.wireOp",EDGE,"E109"),sQuery(id+"F4.wireOp",EDGE,"E110"),sQuery(id+"F4.wireOp",EDGE,"E111"),sQuery(id+"F4.wireOp",EDGE,"E112"),sQuery(id+"F4.wireOp",EDGE,"E113")])]});
            transform(context, id + "F6", {"entities" : qUnion([Q0]), "transformType" : TransformType.TRANSLATION_3D, "dx" : 50.5 * mm, "dy" : 0 * mm, "dz" : 0 * mm, "makeCopy" : true});
        }
        {
            var Q0;
            Q0=qCreatedBy(makeId("Front.planeOp"),FACE);
            var sketch = newSketch(context, id + "F7", { "sketchPlane" : qUnion([Q0])});
            skCircle(sketch, "E114", {"center": v(118.4, 10) * mm, "radius": 2.45 * mm});
            skLineSegment(sketch, "E115.bottom", {"start": v(121.28, 6.2) * mm, "end": v(115.52, 6.2) * mm});
            skLineSegment(sketch, "E115.top", {"start": v(121.28, 13.8) * mm, "end": v(115.52, 13.8) * mm});
            skLineSegment(sketch, "E115.left", {"start": v(122.2, 7.12) * mm, "end": v(122.2, 12.88) * mm});
            skLineSegment(sketch, "E115.right", {"start": v(114.6, 7.12) * mm, "end": v(114.6, 12.88) * mm});
            skLineSegment(sketch, "E116", {"start": v(122.2, 7.12) * mm, "end": v(126.3, 3.02) * mm});
            skLineSegment(sketch, "E117", {"start": v(121.28, 6.2) * mm, "end": v(125.38, 2.1) * mm});
            skLineSegment(sketch, "E118.MirrorCS", {"start": v(121.45, 2.1) * mm, "end": v(125.38, 2.1) * mm});
            skLineSegment(sketch, "E119.MirrorCS", {"start": v(121.45, 0.6) * mm, "end": v(121.45, 2.1) * mm});
            skLineSegment(sketch, "E120.MirrorCS", {"start": v(122, 0) * mm, "end": v(122, 0.6) * mm});
            skLineSegment(sketch, "E121", {"start": v(122, 0) * mm, "end": v(127.8, 0) * mm});
            skLineSegment(sketch, "E122.1.0", {"start": v(115.35, 2.1) * mm, "end": v(111.42, 2.1) * mm});
            skLineSegment(sketch, "E122.1.1", {"start": v(115.35, 0.6) * mm, "end": v(115.35, 2.1) * mm});
            skLineSegment(sketch, "E122.1.2", {"start": v(114.8, 0.6) * mm, "end": v(115.35, 0.6) * mm});
            skLineSegment(sketch, "E122.1.3", {"start": v(109, 0) * mm, "end": v(114.8, 0) * mm});
            skLineSegment(sketch, "E122.1.4", {"start": v(114.8, 0) * mm, "end": v(114.8, 0.6) * mm});
            skLineSegment(sketch, "E122.1.5", {"start": v(115.52, 6.2) * mm, "end": v(111.42, 2.1) * mm});
            skLineSegment(sketch, "E122.1.6", {"start": v(114.6, 7.12) * mm, "end": v(110.5, 3.02) * mm});
            skLineSegment(sketch, "E122.2.0", {"start": v(110.5, 3.02) * mm, "end": v(110.5, 6.95) * mm});
            skLineSegment(sketch, "E122.2.3", {"start": v(108.4, 19.4) * mm, "end": v(108.4, 13.6) * mm});
            skLineSegment(sketch, "E122.2.5", {"start": v(114.6, 12.88) * mm, "end": v(110.5, 16.98) * mm});
            skLineSegment(sketch, "E122.2.6", {"start": v(115.52, 13.8) * mm, "end": v(111.42, 17.9) * mm});
            skLineSegment(sketch, "E122.2.11", {"start": v(109, 20) * mm, "end": v(114.8, 20) * mm});
            skLineSegment(sketch, "E122.3.0", {"start": v(121.45, 17.9) * mm, "end": v(125.38, 17.9) * mm});
            skLineSegment(sketch, "E122.3.1", {"start": v(121.45, 19.4) * mm, "end": v(121.45, 17.9) * mm});
            skLineSegment(sketch, "E122.3.2", {"start": v(122, 19.4) * mm, "end": v(121.45, 19.4) * mm});
            skLineSegment(sketch, "E122.3.3", {"start": v(127.8, 20) * mm, "end": v(122, 20) * mm});
            skLineSegment(sketch, "E122.3.4", {"start": v(122, 20) * mm, "end": v(122, 19.4) * mm});
            skLineSegment(sketch, "E122.3.5", {"start": v(121.28, 13.8) * mm, "end": v(125.38, 17.9) * mm});
            skLineSegment(sketch, "E122.3.6", {"start": v(122.2, 12.88) * mm, "end": v(126.3, 16.98) * mm});
            skArc(sketch, "E123.1.6", {"start": v(108.4, 0.6) * mm, "mid": v(108.58, 0.18) * mm, "end": v(109, 0) * mm});
            skLineSegment(sketch, "E123.1.7", {"start": v(108.4, 6.4) * mm, "end": v(108.4, 0.6) * mm});
            skLineSegment(sketch, "E123.1.8", {"start": v(108.4, 6.4) * mm, "end": v(109, 6.4) * mm});
            skLineSegment(sketch, "E123.1.9", {"start": v(109, 6.4) * mm, "end": v(109, 6.95) * mm});
            skLineSegment(sketch, "E123.1.10", {"start": v(109, 6.95) * mm, "end": v(110.5, 6.95) * mm});
            skLineSegment(sketch, "E123.1.11", {"start": v(110.5, 6.95) * mm, "end": v(110.5, 3.02) * mm});
            skLineSegment(sketch, "E123.2.1", {"start": v(110.5, 13.05) * mm, "end": v(110.5, 16.98) * mm});
            skLineSegment(sketch, "E123.2.2", {"start": v(109, 13.05) * mm, "end": v(110.5, 13.05) * mm});
            skLineSegment(sketch, "E123.2.3", {"start": v(109, 13.6) * mm, "end": v(109, 13.05) * mm});
            skLineSegment(sketch, "E123.2.4", {"start": v(108.4, 13.6) * mm, "end": v(109, 13.6) * mm});
            skArc(sketch, "E123.2.6", {"start": v(109, 20) * mm, "mid": v(108.58, 19.82) * mm, "end": v(108.4, 19.4) * mm});
            skLineSegment(sketch, "E123.2.7", {"start": v(114.8, 20) * mm, "end": v(109, 20) * mm});
            skLineSegment(sketch, "E123.2.8", {"start": v(114.8, 20) * mm, "end": v(114.8, 19.4) * mm});
            skLineSegment(sketch, "E123.2.9", {"start": v(114.8, 19.4) * mm, "end": v(115.35, 19.4) * mm});
            skLineSegment(sketch, "E123.2.10", {"start": v(115.35, 19.4) * mm, "end": v(115.35, 17.9) * mm});
            skLineSegment(sketch, "E123.2.11", {"start": v(115.35, 17.9) * mm, "end": v(111.42, 17.9) * mm});
            skLineSegment(sketch, "E124.trimOffspring", {"start": v(108.4, 6.4) * mm, "end": v(108.4, 3) * mm});
            skLineSegment(sketch, "E125.trimOffspring", {"start": v(125.38, 17.9) * mm, "end": v(121.45, 17.9) * mm});
            skLineSegment(sketch, "E126", {"start": v(122, 0.6) * mm, "end": v(121.45, 0.6) * mm});
            skLineSegment(sketch, "E127.trimOffspring", {"start": v(125.38, 2.1) * mm, "end": v(121.28, 6.2) * mm});
            skLineSegment(sketch, "E128.MirrorCS", {"start": v(141.45, 0.6) * mm, "end": v(141.45, 2.1) * mm});
            skLineSegment(sketch, "E129.MirrorCS", {"start": v(134.8, 19.4) * mm, "end": v(135.35, 19.4) * mm});
            skLineSegment(sketch, "E130.MirrorCS", {"start": v(142, 0.6) * mm, "end": v(141.45, 0.6) * mm});
            skLineSegment(sketch, "E131.MirrorCS", {"start": v(142, 0) * mm, "end": v(142, 0.6) * mm});
            skLineSegment(sketch, "E132.MirrorCS", {"start": v(134.8, 20) * mm, "end": v(134.8, 19.4) * mm});
            skLineSegment(sketch, "E133.MirrorCS", {"start": v(135.35, 19.4) * mm, "end": v(135.35, 17.9) * mm});
            skLineSegment(sketch, "E134.MirrorCS", {"start": v(142, 20) * mm, "end": v(142, 19.4) * mm});
            skArc(sketch, "E135.MirrorCS", {"start": v(147.8, 20) * mm, "mid": v(148.22, 19.82) * mm, "end": v(148.4, 19.4) * mm});
            skLineSegment(sketch, "E136.MirrorCS", {"start": v(148.4, 13.6) * mm, "end": v(147.8, 13.6) * mm});
            skLineSegment(sketch, "E137.MirrorCS", {"start": v(142, 19.4) * mm, "end": v(141.45, 19.4) * mm});
            skLineSegment(sketch, "E138.MirrorCS", {"start": v(148.4, 6.4) * mm, "end": v(147.8, 6.4) * mm});
            skLineSegment(sketch, "E139.MirrorCS", {"start": v(147.8, 13.05) * mm, "end": v(146.3, 13.05) * mm});
            skLineSegment(sketch, "E140.MirrorCS", {"start": v(135.35, 0.6) * mm, "end": v(135.35, 2.1) * mm});
            skLineSegment(sketch, "E141.MirrorCS", {"start": v(141.45, 19.4) * mm, "end": v(141.45, 17.9) * mm});
            skArc(sketch, "E142.MirrorCS", {"start": v(148.4, 0.6) * mm, "mid": v(148.22, 0.18) * mm, "end": v(147.8, 0) * mm});
            skLineSegment(sketch, "E143.MirrorCS", {"start": v(135.35, 17.9) * mm, "end": v(131.42, 17.9) * mm});
            skLineSegment(sketch, "E144.MirrorCS", {"start": v(134.8, 0.6) * mm, "end": v(135.35, 0.6) * mm});
            skLineSegment(sketch, "E145.MirrorCS", {"start": v(147.8, 6.4) * mm, "end": v(147.8, 6.95) * mm});
            skLineSegment(sketch, "E146.MirrorCS", {"start": v(147.8, 6.95) * mm, "end": v(146.3, 6.95) * mm});
            skLineSegment(sketch, "E147.MirrorCS", {"start": v(134.8, 0) * mm, "end": v(134.8, 0.6) * mm});
            skLineSegment(sketch, "E148.MirrorCS", {"start": v(147.8, 13.6) * mm, "end": v(147.8, 13.05) * mm});
            skLineSegment(sketch, "E149.MirrorCS", {"start": v(135.52, 13.8) * mm, "end": v(131.42, 17.9) * mm});
            skPoint(sketch, "E150.MirrorP", {"position": v(138.4, 10) * mm});
            skLineSegment(sketch, "E151.MirrorCS", {"start": v(146.3, 13.05) * mm, "end": v(146.3, 16.98) * mm});
            skLineSegment(sketch, "E152.MirrorCS", {"start": v(147.8, 0) * mm, "end": v(142, 0) * mm});
            skLineSegment(sketch, "E153.MirrorCS", {"start": v(141.45, 17.9) * mm, "end": v(145.38, 17.9) * mm});
            skLineSegment(sketch, "E154.MirrorCS", {"start": v(142.2, 7.12) * mm, "end": v(146.3, 3.02) * mm});
            skLineSegment(sketch, "E155.MirrorCS", {"start": v(141.45, 2.1) * mm, "end": v(145.38, 2.1) * mm});
            skLineSegment(sketch, "E156.MirrorCS", {"start": v(142.2, 12.88) * mm, "end": v(146.3, 16.98) * mm});
            skLineSegment(sketch, "E157.MirrorCS", {"start": v(146.3, 6.95) * mm, "end": v(146.3, 3.02) * mm});
            skLineSegment(sketch, "E158.MirrorCS", {"start": v(141.28, 6.2) * mm, "end": v(145.38, 2.1) * mm});
            skLineSegment(sketch, "E159.MirrorCS", {"start": v(131.42, 17.9) * mm, "end": v(135.35, 17.9) * mm});
            skLineSegment(sketch, "E160.MirrorCS", {"start": v(142, 20) * mm, "end": v(147.8, 20) * mm});
            skLineSegment(sketch, "E161.MirrorCS", {"start": v(141.28, 13.8) * mm, "end": v(145.38, 17.9) * mm});
            skLineSegment(sketch, "E162.MirrorCS", {"start": v(148.4, 6.4) * mm, "end": v(148.4, 3) * mm});
            skLineSegment(sketch, "E163.MirrorCS", {"start": v(129, 20) * mm, "end": v(134.8, 20) * mm});
            skLineSegment(sketch, "E164.MirrorCS", {"start": v(148.4, 19.4) * mm, "end": v(148.4, 13.6) * mm});
            skLineSegment(sketch, "E165.MirrorCS", {"start": v(131.42, 2.1) * mm, "end": v(135.52, 6.2) * mm});
            skLineSegment(sketch, "E166.MirrorCS", {"start": v(146.3, 3.02) * mm, "end": v(146.3, 6.95) * mm});
            skLineSegment(sketch, "E167.MirrorCS", {"start": v(134.6, 12.88) * mm, "end": v(130.5, 16.98) * mm});
            skLineSegment(sketch, "E168.MirrorCS", {"start": v(134.8, 0) * mm, "end": v(129, 0) * mm});
            skCircle(sketch, "E169.MirrorC", {"center": v(138.4, 10) * mm, "radius": 2.45 * mm});
            skLineSegment(sketch, "E170.MirrorCS", {"start": v(135.52, 13.8) * mm, "end": v(141.28, 13.8) * mm});
            skLineSegment(sketch, "E171.MirrorCS", {"start": v(134.6, 7.12) * mm, "end": v(134.6, 12.88) * mm});
            skLineSegment(sketch, "E172.MirrorCS", {"start": v(142.2, 7.12) * mm, "end": v(142.2, 12.88) * mm});
            skLineSegment(sketch, "E173.MirrorCS", {"start": v(134.6, 7.12) * mm, "end": v(130.5, 3.02) * mm});
            skLineSegment(sketch, "E174.MirrorCS", {"start": v(135.52, 6.2) * mm, "end": v(131.42, 2.1) * mm});
            skLineSegment(sketch, "E175.MirrorCS", {"start": v(135.35, 2.1) * mm, "end": v(131.42, 2.1) * mm});
            skLineSegment(sketch, "E176.MirrorCS", {"start": v(148.4, 6.4) * mm, "end": v(148.4, 0.6) * mm});
            skLineSegment(sketch, "E177.MirrorCS", {"start": v(147.8, 20) * mm, "end": v(142, 20) * mm});
            skLineSegment(sketch, "E178.MirrorCS", {"start": v(135.52, 6.2) * mm, "end": v(141.28, 6.2) * mm});
            skLineSegment(sketch, "E179", {"start": v(127.22, 17.9) * mm, "end": v(129.58, 17.9) * mm});
            skLineSegment(sketch, "E180", {"start": v(126.3, 16.98) * mm, "end": v(127.22, 17.9) * mm});
            skLineSegment(sketch, "E181", {"start": v(130.5, 16.98) * mm, "end": v(129.58, 17.9) * mm});
            skLineSegment(sketch, "E182", {"start": v(127.8, 20) * mm, "end": v(129, 20) * mm});
            skPoint(sketch, "E123.3.6.start.orphan", {"position": v(128.4, 19.4) * mm});
            skLineSegment(sketch, "E183", {"start": v(127.22, 2.1) * mm, "end": v(129.58, 2.1) * mm});
            skLineSegment(sketch, "E184", {"start": v(130.5, 3.02) * mm, "end": v(129.58, 2.1) * mm});
            skLineSegment(sketch, "E185", {"start": v(126.3, 3.02) * mm, "end": v(127.22, 2.1) * mm});
            skLineSegment(sketch, "E186", {"start": v(127.8, 0) * mm, "end": v(129, 0) * mm});
            skSolve(sketch);
        }
        {
            var Q0;
            Q0=makeQuery(id+"F7.imprint","IMPRINT",FACE,{"disambiguationData":[TD([[makeQuery(id+"F7.imprint","IMPRINT",EDGE,{"derivedFrom":sQuery(id+"F7.wireOp",EDGE,"E114")}),-1.0]])]});
            extrude(context, id + "F8", {"entities" : qUnion([Q0]), "oppositeDirection" : true, "depth" : 400 * mm});
        }
        {
            var Q0;
            Q0=qCreatedBy(makeId("Front.planeOp"),FACE);
            var sketch = newSketch(context, id + "F9", { "sketchPlane" : qUnion([Q0])});
            skCircle(sketch, "E187", {"center": v(180.05, 9.57) * mm, "radius": 2.45 * mm});
            skLineSegment(sketch, "E188.bottom", {"start": v(182.93, 5.77) * mm, "end": v(177.17, 5.77) * mm});
            skLineSegment(sketch, "E188.top", {"start": v(182.93, 13.37) * mm, "end": v(177.17, 13.37) * mm});
            skLineSegment(sketch, "E188.left", {"start": v(183.85, 6.7) * mm, "end": v(183.85, 12.46) * mm});
            skLineSegment(sketch, "E188.right", {"start": v(176.25, 6.7) * mm, "end": v(176.25, 12.46) * mm});
            skLineSegment(sketch, "E189", {"start": v(183.85, 6.7) * mm, "end": v(187.95, 2.6) * mm});
            skLineSegment(sketch, "E190", {"start": v(182.93, 5.77) * mm, "end": v(187.03, 1.67) * mm});
            skLineSegment(sketch, "E191.MirrorCS", {"start": v(183.1, 1.67) * mm, "end": v(187.03, 1.67) * mm});
            skLineSegment(sketch, "E192.MirrorCS", {"start": v(183.1, 0.17) * mm, "end": v(183.1, 1.67) * mm});
            skLineSegment(sketch, "E193.MirrorCS", {"start": v(183.65, -0.43) * mm, "end": v(183.65, 0.17) * mm});
            skLineSegment(sketch, "E194", {"start": v(183.65, -0.43) * mm, "end": v(189.45, -0.43) * mm});
            skLineSegment(sketch, "E195.1.0", {"start": v(177, 1.67) * mm, "end": v(173.07, 1.67) * mm});
            skLineSegment(sketch, "E195.1.1", {"start": v(177, 0.17) * mm, "end": v(177, 1.67) * mm});
            skLineSegment(sketch, "E195.1.2", {"start": v(176.45, 0.17) * mm, "end": v(177, 0.17) * mm});
            skLineSegment(sketch, "E195.1.3", {"start": v(170.65, -0.43) * mm, "end": v(176.45, -0.43) * mm});
            skLineSegment(sketch, "E195.1.4", {"start": v(176.45, -0.43) * mm, "end": v(176.45, 0.17) * mm});
            skLineSegment(sketch, "E195.1.5", {"start": v(177.17, 5.77) * mm, "end": v(173.07, 1.67) * mm});
            skLineSegment(sketch, "E195.1.6", {"start": v(176.25, 6.7) * mm, "end": v(172.15, 2.6) * mm});
            skLineSegment(sketch, "E195.2.0", {"start": v(172.15, 2.6) * mm, "end": v(172.15, 6.52) * mm});
            skLineSegment(sketch, "E195.2.3", {"start": v(170.05, 18.97) * mm, "end": v(170.05, 13.17) * mm});
            skLineSegment(sketch, "E195.2.5", {"start": v(176.25, 12.46) * mm, "end": v(172.15, 16.56) * mm});
            skLineSegment(sketch, "E195.2.6", {"start": v(177.17, 13.37) * mm, "end": v(173.07, 17.47) * mm});
            skLineSegment(sketch, "E195.2.11", {"start": v(170.65, 19.57) * mm, "end": v(176.45, 19.57) * mm});
            skLineSegment(sketch, "E195.3.0", {"start": v(183.1, 17.47) * mm, "end": v(187.03, 17.47) * mm});
            skLineSegment(sketch, "E195.3.1", {"start": v(183.1, 18.97) * mm, "end": v(183.1, 17.47) * mm});
            skLineSegment(sketch, "E195.3.2", {"start": v(183.65, 18.97) * mm, "end": v(183.1, 18.97) * mm});
            skLineSegment(sketch, "E195.3.3", {"start": v(189.45, 19.57) * mm, "end": v(183.65, 19.57) * mm});
            skLineSegment(sketch, "E195.3.4", {"start": v(183.65, 19.57) * mm, "end": v(183.65, 18.97) * mm});
            skLineSegment(sketch, "E195.3.5", {"start": v(182.93, 13.37) * mm, "end": v(187.03, 17.47) * mm});
            skLineSegment(sketch, "E195.3.6", {"start": v(183.85, 12.46) * mm, "end": v(187.95, 16.56) * mm});
            skArc(sketch, "E196.1.6", {"start": v(170.05, 0.17) * mm, "mid": v(170.23, -0.25) * mm, "end": v(170.65, -0.43) * mm});
            skLineSegment(sketch, "E196.1.7", {"start": v(170.05, 5.97) * mm, "end": v(170.05, 0.17) * mm});
            skLineSegment(sketch, "E196.1.8", {"start": v(170.05, 5.97) * mm, "end": v(170.65, 5.97) * mm});
            skLineSegment(sketch, "E196.1.9", {"start": v(170.65, 5.97) * mm, "end": v(170.65, 6.52) * mm});
            skLineSegment(sketch, "E196.1.10", {"start": v(170.65, 6.52) * mm, "end": v(172.15, 6.52) * mm});
            skLineSegment(sketch, "E196.1.11", {"start": v(172.15, 6.52) * mm, "end": v(172.15, 2.6) * mm});
            skLineSegment(sketch, "E196.2.1", {"start": v(172.15, 12.62) * mm, "end": v(172.15, 16.56) * mm});
            skLineSegment(sketch, "E196.2.2", {"start": v(170.65, 12.62) * mm, "end": v(172.15, 12.62) * mm});
            skLineSegment(sketch, "E196.2.3", {"start": v(170.65, 13.17) * mm, "end": v(170.65, 12.62) * mm});
            skLineSegment(sketch, "E196.2.4", {"start": v(170.05, 13.17) * mm, "end": v(170.65, 13.17) * mm});
            skArc(sketch, "E196.2.6", {"start": v(170.65, 19.57) * mm, "mid": v(170.23, 19.4) * mm, "end": v(170.05, 18.97) * mm});
            skLineSegment(sketch, "E196.2.7", {"start": v(176.45, 19.57) * mm, "end": v(170.65, 19.57) * mm});
            skLineSegment(sketch, "E196.2.8", {"start": v(176.45, 19.57) * mm, "end": v(176.45, 18.97) * mm});
            skLineSegment(sketch, "E196.2.9", {"start": v(176.45, 18.97) * mm, "end": v(177, 18.97) * mm});
            skLineSegment(sketch, "E196.2.10", {"start": v(177, 18.97) * mm, "end": v(177, 17.47) * mm});
            skLineSegment(sketch, "E196.2.11", {"start": v(177, 17.47) * mm, "end": v(173.07, 17.47) * mm});
            skLineSegment(sketch, "E197.trimOffspring", {"start": v(170.05, 5.97) * mm, "end": v(170.05, 2.57) * mm});
            skLineSegment(sketch, "E198.trimOffspring", {"start": v(187.03, 17.47) * mm, "end": v(183.1, 17.47) * mm});
            skLineSegment(sketch, "E199", {"start": v(183.65, 0.17) * mm, "end": v(183.1, 0.17) * mm});
            skLineSegment(sketch, "E200.trimOffspring", {"start": v(187.03, 1.67) * mm, "end": v(182.93, 5.77) * mm});
            skLineSegment(sketch, "E201.MirrorCS", {"start": v(203.1, 0.17) * mm, "end": v(203.1, 1.67) * mm});
            skLineSegment(sketch, "E202.MirrorCS", {"start": v(196.45, 18.97) * mm, "end": v(197, 18.97) * mm});
            skLineSegment(sketch, "E203.MirrorCS", {"start": v(203.65, 0.17) * mm, "end": v(203.1, 0.17) * mm});
            skLineSegment(sketch, "E204.MirrorCS", {"start": v(203.65, -0.43) * mm, "end": v(203.65, 0.17) * mm});
            skLineSegment(sketch, "E205.MirrorCS", {"start": v(196.45, 19.57) * mm, "end": v(196.45, 18.97) * mm});
            skLineSegment(sketch, "E206.MirrorCS", {"start": v(197, 18.97) * mm, "end": v(197, 17.47) * mm});
            skLineSegment(sketch, "E207.MirrorCS", {"start": v(203.65, 19.57) * mm, "end": v(203.65, 18.97) * mm});
            skArc(sketch, "E208.MirrorCS", {"start": v(209.45, 19.57) * mm, "mid": v(209.87, 19.4) * mm, "end": v(210.05, 18.97) * mm});
            skLineSegment(sketch, "E209.MirrorCS", {"start": v(210.05, 13.17) * mm, "end": v(209.45, 13.17) * mm});
            skLineSegment(sketch, "E210.MirrorCS", {"start": v(203.65, 18.97) * mm, "end": v(203.1, 18.97) * mm});
            skLineSegment(sketch, "E211.MirrorCS", {"start": v(210.05, 5.97) * mm, "end": v(209.45, 5.97) * mm});
            skLineSegment(sketch, "E212.MirrorCS", {"start": v(209.45, 12.62) * mm, "end": v(207.95, 12.62) * mm});
            skLineSegment(sketch, "E213.MirrorCS", {"start": v(197, 0.17) * mm, "end": v(197, 1.67) * mm});
            skLineSegment(sketch, "E214.MirrorCS", {"start": v(203.1, 18.97) * mm, "end": v(203.1, 17.47) * mm});
            skArc(sketch, "E215.MirrorCS", {"start": v(210.05, 0.17) * mm, "mid": v(209.87, -0.25) * mm, "end": v(209.45, -0.43) * mm});
            skLineSegment(sketch, "E216.MirrorCS", {"start": v(197, 17.47) * mm, "end": v(193.07, 17.47) * mm});
            skLineSegment(sketch, "E217.MirrorCS", {"start": v(196.45, 0.17) * mm, "end": v(197, 0.17) * mm});
            skLineSegment(sketch, "E218.MirrorCS", {"start": v(209.45, 5.97) * mm, "end": v(209.45, 6.52) * mm});
            skLineSegment(sketch, "E219.MirrorCS", {"start": v(209.45, 6.52) * mm, "end": v(207.95, 6.52) * mm});
            skLineSegment(sketch, "E220.MirrorCS", {"start": v(196.45, -0.43) * mm, "end": v(196.45, 0.17) * mm});
            skLineSegment(sketch, "E221.MirrorCS", {"start": v(209.45, 13.17) * mm, "end": v(209.45, 12.62) * mm});
            skLineSegment(sketch, "E222.MirrorCS", {"start": v(197.17, 13.37) * mm, "end": v(193.07, 17.47) * mm});
            skPoint(sketch, "E223.MirrorP", {"position": v(200.05, 9.57) * mm});
            skLineSegment(sketch, "E224.MirrorCS", {"start": v(207.95, 12.62) * mm, "end": v(207.95, 16.56) * mm});
            skLineSegment(sketch, "E225.MirrorCS", {"start": v(209.45, -0.43) * mm, "end": v(203.65, -0.43) * mm});
            skLineSegment(sketch, "E226.MirrorCS", {"start": v(203.1, 17.47) * mm, "end": v(207.03, 17.47) * mm});
            skLineSegment(sketch, "E227.MirrorCS", {"start": v(203.85, 6.7) * mm, "end": v(207.95, 2.6) * mm});
            skLineSegment(sketch, "E228.MirrorCS", {"start": v(203.1, 1.67) * mm, "end": v(207.03, 1.67) * mm});
            skLineSegment(sketch, "E229.MirrorCS", {"start": v(203.85, 12.46) * mm, "end": v(207.95, 16.56) * mm});
            skLineSegment(sketch, "E230.MirrorCS", {"start": v(207.95, 6.52) * mm, "end": v(207.95, 2.6) * mm});
            skLineSegment(sketch, "E231.MirrorCS", {"start": v(202.93, 5.77) * mm, "end": v(207.03, 1.67) * mm});
            skLineSegment(sketch, "E232.MirrorCS", {"start": v(193.07, 17.47) * mm, "end": v(197, 17.47) * mm});
            skLineSegment(sketch, "E233.MirrorCS", {"start": v(203.65, 19.57) * mm, "end": v(209.45, 19.57) * mm});
            skLineSegment(sketch, "E234.MirrorCS", {"start": v(202.93, 13.37) * mm, "end": v(207.03, 17.47) * mm});
            skLineSegment(sketch, "E235.MirrorCS", {"start": v(210.05, 5.97) * mm, "end": v(210.05, 2.57) * mm});
            skLineSegment(sketch, "E236.MirrorCS", {"start": v(190.65, 19.57) * mm, "end": v(196.45, 19.57) * mm});
            skLineSegment(sketch, "E237.MirrorCS", {"start": v(210.05, 18.97) * mm, "end": v(210.05, 13.17) * mm});
            skLineSegment(sketch, "E238.MirrorCS", {"start": v(193.07, 1.67) * mm, "end": v(197.17, 5.77) * mm});
            skLineSegment(sketch, "E239.MirrorCS", {"start": v(207.95, 2.6) * mm, "end": v(207.95, 6.52) * mm});
            skLineSegment(sketch, "E240.MirrorCS", {"start": v(196.25, 12.46) * mm, "end": v(192.15, 16.56) * mm});
            skLineSegment(sketch, "E241.MirrorCS", {"start": v(196.45, -0.43) * mm, "end": v(190.65, -0.43) * mm});
            skCircle(sketch, "E242.MirrorC", {"center": v(200.05, 9.57) * mm, "radius": 2.45 * mm});
            skLineSegment(sketch, "E243.MirrorCS", {"start": v(197.17, 13.37) * mm, "end": v(202.93, 13.37) * mm});
            skLineSegment(sketch, "E244.MirrorCS", {"start": v(196.25, 6.7) * mm, "end": v(196.25, 12.46) * mm});
            skLineSegment(sketch, "E245.MirrorCS", {"start": v(203.85, 6.7) * mm, "end": v(203.85, 12.46) * mm});
            skLineSegment(sketch, "E246.MirrorCS", {"start": v(196.25, 6.7) * mm, "end": v(192.15, 2.6) * mm});
            skLineSegment(sketch, "E247.MirrorCS", {"start": v(197.17, 5.77) * mm, "end": v(193.07, 1.67) * mm});
            skLineSegment(sketch, "E248.MirrorCS", {"start": v(197, 1.67) * mm, "end": v(193.07, 1.67) * mm});
            skLineSegment(sketch, "E249.MirrorCS", {"start": v(210.05, 5.97) * mm, "end": v(210.05, 0.17) * mm});
            skLineSegment(sketch, "E250.MirrorCS", {"start": v(209.45, 19.57) * mm, "end": v(203.65, 19.57) * mm});
            skLineSegment(sketch, "E251.MirrorCS", {"start": v(197.17, 5.77) * mm, "end": v(202.93, 5.77) * mm});
            skLineSegment(sketch, "E252", {"start": v(188.87, 17.47) * mm, "end": v(191.23, 17.47) * mm});
            skLineSegment(sketch, "E253", {"start": v(187.95, 16.56) * mm, "end": v(188.87, 17.47) * mm});
            skLineSegment(sketch, "E254", {"start": v(192.15, 16.56) * mm, "end": v(191.23, 17.47) * mm});
            skLineSegment(sketch, "E255", {"start": v(189.45, 19.57) * mm, "end": v(190.65, 19.57) * mm});
            skPoint(sketch, "E196.3.6.start.orphan", {"position": v(190.05, 18.97) * mm});
            skLineSegment(sketch, "E256", {"start": v(188.87, 1.67) * mm, "end": v(191.23, 1.67) * mm});
            skLineSegment(sketch, "E257", {"start": v(192.15, 2.6) * mm, "end": v(191.23, 1.67) * mm});
            skLineSegment(sketch, "E258", {"start": v(187.95, 2.6) * mm, "end": v(188.87, 1.67) * mm});
            skLineSegment(sketch, "E259", {"start": v(189.45, -0.43) * mm, "end": v(190.65, -0.43) * mm});
            skSolve(sketch);
        }
        {
            var Q0;
            Q0=makeQuery(id+"F9.imprint","IMPRINT",FACE,{"disambiguationData":[TD([[makeQuery(id+"F9.imprint","IMPRINT",EDGE,{"derivedFrom":sQuery(id+"F9.wireOp",EDGE,"E187")}),-1.0]])]});
            extrude(context, id + "F10", {"entities" : qUnion([Q0]), "oppositeDirection" : true, "depth" : 420 * mm});
        }
        {
            var Q0;
            Q0=makeQuery(id+"F10.opExtrude","SWEPT_BODY",BODY,{"disambiguationData":[OSD([sQuery(id+"F9.wireOp",EDGE,"E187"),sQuery(id+"F9.wireOp",EDGE,"E188.bottom"),sQuery(id+"F9.wireOp",EDGE,"E188.top"),sQuery(id+"F9.wireOp",EDGE,"E188.left"),sQuery(id+"F9.wireOp",EDGE,"E188.right"),sQuery(id+"F9.wireOp",EDGE,"E189"),sQuery(id+"F9.wireOp",EDGE,"E191.MirrorCS"),sQuery(id+"F9.wireOp",EDGE,"E192.MirrorCS"),sQuery(id+"F9.wireOp",EDGE,"E193.MirrorCS"),sQuery(id+"F9.wireOp",EDGE,"E194"),sQuery(id+"F9.wireOp",EDGE,"E195.3.6"),sQuery(id+"F9.wireOp",EDGE,"E195.1.0"),sQuery(id+"F9.wireOp",EDGE,"E195.1.1"),sQuery(id+"F9.wireOp",EDGE,"E195.1.2"),sQuery(id+"F9.wireOp",EDGE,"E195.1.4"),sQuery(id+"F9.wireOp",EDGE,"E195.1.3"),sQuery(id+"F9.wireOp",EDGE,"E196.1.6"),sQuery(id+"F9.wireOp",EDGE,"E196.1.7"),sQuery(id+"F9.wireOp",EDGE,"E196.1.8"),sQuery(id+"F9.wireOp",EDGE,"E196.1.9"),sQuery(id+"F9.wireOp",EDGE,"E196.1.10"),sQuery(id+"F9.wireOp",EDGE,"E196.1.11"),sQuery(id+"F9.wireOp",EDGE,"E195.1.6"),sQuery(id+"F9.wireOp",EDGE,"E196.2.2"),sQuery(id+"F9.wireOp",EDGE,"E196.2.3"),sQuery(id+"F9.wireOp",EDGE,"E196.2.4"),sQuery(id+"F9.wireOp",EDGE,"E195.2.3"),sQuery(id+"F9.wireOp",EDGE,"E196.2.6"),sQuery(id+"F9.wireOp",EDGE,"E196.2.7"),sQuery(id+"F9.wireOp",EDGE,"E196.2.8"),sQuery(id+"F9.wireOp",EDGE,"E196.2.9"),sQuery(id+"F9.wireOp",EDGE,"E196.2.10"),sQuery(id+"F9.wireOp",EDGE,"E195.2.6"),sQuery(id+"F9.wireOp",EDGE,"E195.3.5"),sQuery(id+"F9.wireOp",EDGE,"E195.3.1"),sQuery(id+"F9.wireOp",EDGE,"E195.3.2"),sQuery(id+"F9.wireOp",EDGE,"E195.3.4"),sQuery(id+"F9.wireOp",EDGE,"E195.3.3"),sQuery(id+"F9.wireOp",EDGE,"E197.trimOffspring"),sQuery(id+"F9.wireOp",EDGE,"E196.2.1"),sQuery(id+"F9.wireOp",EDGE,"E196.2.11"),sQuery(id+"F9.wireOp",EDGE,"E195.2.5"),sQuery(id+"F9.wireOp",EDGE,"E195.1.5"),sQuery(id+"F9.wireOp",EDGE,"E198.trimOffspring"),sQuery(id+"F9.wireOp",EDGE,"E199"),sQuery(id+"F9.wireOp",EDGE,"E200.trimOffspring"),sQuery(id+"F9.wireOp",EDGE,"E201.MirrorCS"),sQuery(id+"F9.wireOp",EDGE,"E203.MirrorCS"),sQuery(id+"F9.wireOp",EDGE,"E205.MirrorCS"),sQuery(id+"F9.wireOp",EDGE,"E202.MirrorCS"),sQuery(id+"F9.wireOp",EDGE,"E206.MirrorCS"),sQuery(id+"F9.wireOp",EDGE,"E204.MirrorCS"),sQuery(id+"F9.wireOp",EDGE,"E207.MirrorCS"),sQuery(id+"F9.wireOp",EDGE,"E208.MirrorCS"),sQuery(id+"F9.wireOp",EDGE,"E209.MirrorCS"),sQuery(id+"F9.wireOp",EDGE,"E210.MirrorCS"),sQuery(id+"F9.wireOp",EDGE,"E211.MirrorCS"),sQuery(id+"F9.wireOp",EDGE,"E212.MirrorCS"),sQuery(id+"F9.wireOp",EDGE,"E213.MirrorCS"),sQuery(id+"F9.wireOp",EDGE,"E214.MirrorCS"),sQuery(id+"F9.wireOp",EDGE,"E215.MirrorCS"),sQuery(id+"F9.wireOp",EDGE,"E217.MirrorCS"),sQuery(id+"F9.wireOp",EDGE,"E218.MirrorCS"),sQuery(id+"F9.wireOp",EDGE,"E219.MirrorCS"),sQuery(id+"F9.wireOp",EDGE,"E220.MirrorCS"),sQuery(id+"F9.wireOp",EDGE,"E221.MirrorCS"),sQuery(id+"F9.wireOp",EDGE,"E239.MirrorCS"),sQuery(id+"F9.wireOp",EDGE,"E237.MirrorCS"),sQuery(id+"F9.wireOp",EDGE,"E227.MirrorCS"),sQuery(id+"F9.wireOp",EDGE,"E240.MirrorCS"),sQuery(id+"F9.wireOp",EDGE,"E241.MirrorCS"),sQuery(id+"F9.wireOp",EDGE,"E242.MirrorC"),sQuery(id+"F9.wireOp",EDGE,"E224.MirrorCS"),sQuery(id+"F9.wireOp",EDGE,"E243.MirrorCS"),sQuery(id+"F9.wireOp",EDGE,"E244.MirrorCS"),sQuery(id+"F9.wireOp",EDGE,"E245.MirrorCS"),sQuery(id+"F9.wireOp",EDGE,"E246.MirrorCS"),sQuery(id+"F9.wireOp",EDGE,"E247.MirrorCS"),sQuery(id+"F9.wireOp",EDGE,"E234.MirrorCS"),sQuery(id+"F9.wireOp",EDGE,"E248.MirrorCS"),sQuery(id+"F9.wireOp",EDGE,"E216.MirrorCS"),sQuery(id+"F9.wireOp",EDGE,"E249.MirrorCS"),sQuery(id+"F9.wireOp",EDGE,"E228.MirrorCS"),sQuery(id+"F9.wireOp",EDGE,"E229.MirrorCS"),sQuery(id+"F9.wireOp",EDGE,"E231.MirrorCS"),sQuery(id+"F9.wireOp",EDGE,"E226.MirrorCS"),sQuery(id+"F9.wireOp",EDGE,"E222.MirrorCS"),sQuery(id+"F9.wireOp",EDGE,"E225.MirrorCS"),sQuery(id+"F9.wireOp",EDGE,"E236.MirrorCS"),sQuery(id+"F9.wireOp",EDGE,"E250.MirrorCS"),sQuery(id+"F9.wireOp",EDGE,"E251.MirrorCS"),sQuery(id+"F9.wireOp",EDGE,"E252"),sQuery(id+"F9.wireOp",EDGE,"E253"),sQuery(id+"F9.wireOp",EDGE,"E254"),sQuery(id+"F9.wireOp",EDGE,"E255"),sQuery(id+"F9.wireOp",EDGE,"E256"),sQuery(id+"F9.wireOp",EDGE,"E257"),sQuery(id+"F9.wireOp",EDGE,"E258"),sQuery(id+"F9.wireOp",EDGE,"E259")])]});
            transform(context, id + "F11", {"entities" : qUnion([Q0]), "transformType" : TransformType.TRANSLATION_3D, "dx" : 52.5 * mm, "dy" : 0 * mm, "dz" : 0 * mm, "makeCopy" : true});
        }
    });
